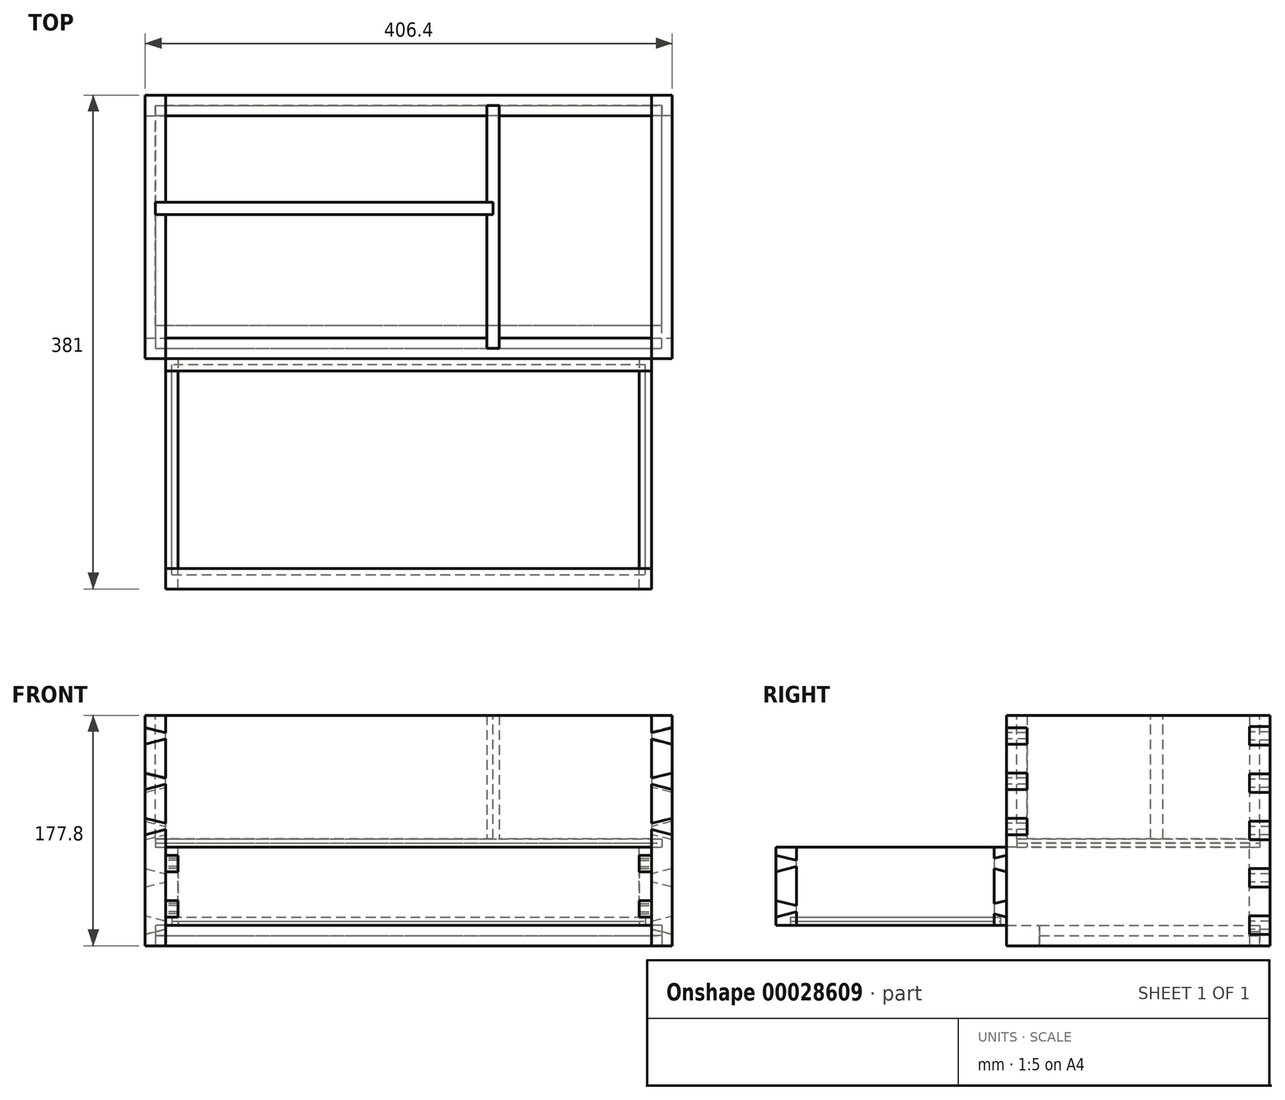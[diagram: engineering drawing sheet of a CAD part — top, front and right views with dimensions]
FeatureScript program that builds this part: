
annotation { "Feature Type Name" : "Feature", "Feature Type Description" : "" }
export const myFeature = defineFeature(function(context is Context, id is Id, definition is map)
    precondition{}
    {
        {
            var Q0;
            Q0=qCreatedBy(makeId("Front.planeOp"),FACE);
            var sketch = newSketch(context, id + "F0", { "sketchPlane" : qUnion([Q0])});
            skLineSegment(sketch, "E0.bottom", {"start": v(0, 0) * mm, "end": v(406.4, 0) * mm});
            skLineSegment(sketch, "E0.top", {"start": v(0, 177.8) * mm, "end": v(406.4, 177.8) * mm});
            skLineSegment(sketch, "E0.left", {"start": v(0, 0) * mm, "end": v(0, 177.8) * mm});
            skLineSegment(sketch, "E0.right", {"start": v(406.4, 0) * mm, "end": v(406.4, 177.8) * mm});
            skSolve(sketch);
        }
        {
            var Q0;
            Q0 = qSketchRegion(id + "F0", true);
            extrude(context, id + "F1", {"entities" : qUnion([Q0]), "depth" : 15.88 * mm});
        }
        {
            var Q0;
            Q0=qCreatedBy(makeId("Front.planeOp"),FACE);
            cPlane(context, id + "F2", {"entities" : qUnion([Q0]), "cplaneType" : CPlaneType.OFFSET, "offset" : 203.2 * mm, "width" : 152.4 * mm, "height" : 152.4 * mm});
        }
        {
            var Q0;
            Q0=qCreatedBy(id+"F2.planeOp",FACE);
            var sketch = newSketch(context, id + "F3", { "sketchPlane" : qUnion([Q0])});
            skLineSegment(sketch, "E1.0", {"start": v(0, 76.2) * mm, "end": v(0, 177.8) * mm});
            skLineSegment(sketch, "E1.1", {"start": v(0, 177.8) * mm, "end": v(406.4, 177.8) * mm});
            skLineSegment(sketch, "E1.2", {"start": v(406.4, 76.2) * mm, "end": v(406.4, 177.8) * mm});
            skLineSegment(sketch, "E2", {"start": v(0, 76.2) * mm, "end": v(406.4, 76.2) * mm});
            skPoint(sketch, "E3.orphan", {"position": v(406.4, 0) * mm});
            skPoint(sketch, "E4.orphan", {"position": v(0, 0) * mm});
            skSolve(sketch);
        }
        {
            var Q0;
            Q0 = qSketchRegion(id + "F3", true);
            extrude(context, id + "F4", {"entities" : qUnion([Q0]), "oppositeDirection" : true, "depth" : 15.88 * mm});
        }
        {
            var Q0;
            Q0=makeQuery(id+"F4.opExtrude","CAP_FACE",FACE,{"disambiguationData":[OSD([sQuery(id+"F3.wireOp",EDGE,"E1.0"),sQuery(id+"F3.wireOp",EDGE,"E1.1"),sQuery(id+"F3.wireOp",EDGE,"E1.2"),sQuery(id+"F3.wireOp",EDGE,"E2")])],"isStart":true});
            var sketch = newSketch(context, id + "F5", { "sketchPlane" : qUnion([Q0])});
            skLineSegment(sketch, "E5", {"start": v(390.53, 177.8) * mm, "end": v(390.53, 164.32) * mm, "construction": true});
            skLineSegment(sketch, "E6", {"start": v(406.4, 168.28) * mm, "end": v(390.52, 164.32) * mm});
            skLineSegment(sketch, "E7", {"start": v(390.52, 159.53) * mm, "end": v(406.4, 155.58) * mm});
            skLineSegment(sketch, "E8.0.1.0", {"start": v(406.4, 133.35) * mm, "end": v(390.53, 129.4) * mm});
            skLineSegment(sketch, "E8.0.1.2", {"start": v(390.53, 124.6) * mm, "end": v(406.4, 120.65) * mm});
            skLineSegment(sketch, "E8.0.1.3", {"start": v(406.4, 120.65) * mm, "end": v(406.4, 133.35) * mm});
            skLineSegment(sketch, "E8.0.2.0", {"start": v(406.4, 98.42) * mm, "end": v(390.53, 94.47) * mm});
            skLineSegment(sketch, "E8.0.2.2", {"start": v(390.53, 89.68) * mm, "end": v(406.4, 85.72) * mm});
            skLineSegment(sketch, "E8.direction2", {"start": v(390.52, 159.53) * mm, "end": v(390.52, 129.4) * mm, "construction": true});
            skLineSegment(sketch, "E9", {"start": v(390.53, 164.32) * mm, "end": v(390.53, 177.8) * mm});
            skLineSegment(sketch, "E10", {"start": v(406.4, 177.8) * mm, "end": v(406.4, 168.28) * mm});
            skLineSegment(sketch, "E11", {"start": v(390.53, 159.53) * mm, "end": v(390.53, 129.4) * mm});
            skLineSegment(sketch, "E12", {"start": v(390.53, 124.6) * mm, "end": v(390.53, 94.47) * mm});
            skLineSegment(sketch, "E13", {"start": v(390.53, 89.68) * mm, "end": v(390.53, 76.2) * mm});
            skLineSegment(sketch, "E14", {"start": v(406.4, 76.2) * mm, "end": v(406.4, 85.72) * mm});
            skLineSegment(sketch, "E15", {"start": v(406.4, 98.42) * mm, "end": v(406.4, 120.65) * mm});
            skLineSegment(sketch, "E16", {"start": v(406.4, 133.35) * mm, "end": v(406.4, 155.58) * mm});
            skLineSegment(sketch, "E17.trimOffspring", {"start": v(390.53, 159.53) * mm, "end": v(390.53, 76.2) * mm, "construction": true});
            skLineSegment(sketch, "E18", {"start": v(203.2, 177.8) * mm, "end": v(203.2, 76.2) * mm, "construction": true});
            skLineSegment(sketch, "E19.MirrorCS", {"start": v(15.88, 159.53) * mm, "end": v(15.88, 129.4) * mm});
            skLineSegment(sketch, "E20.MirrorCS", {"start": v(15.88, 89.68) * mm, "end": v(15.88, 76.2) * mm});
            skLineSegment(sketch, "E21.MirrorCS", {"start": v(15.88, 89.68) * mm, "end": v(0, 85.73) * mm});
            skLineSegment(sketch, "E22.MirrorCS", {"start": v(15.88, 177.8) * mm, "end": v(15.88, 164.32) * mm});
            skLineSegment(sketch, "E23.MirrorCS", {"start": v(15.88, 124.6) * mm, "end": v(0, 120.65) * mm});
            skLineSegment(sketch, "E24.MirrorCS", {"start": v(0, 76.2) * mm, "end": v(0, 85.73) * mm});
            skLineSegment(sketch, "E25.MirrorCS", {"start": v(15.88, 124.6) * mm, "end": v(15.88, 94.47) * mm});
            skLineSegment(sketch, "E26.MirrorCS", {"start": v(0, 133.35) * mm, "end": v(0, 155.58) * mm});
            skLineSegment(sketch, "E27.MirrorCS", {"start": v(0, 177.8) * mm, "end": v(0, 168.28) * mm});
            skLineSegment(sketch, "E28.MirrorCS", {"start": v(15.88, 164.32) * mm, "end": v(15.88, 177.8) * mm});
            skLineSegment(sketch, "E29.MirrorCS", {"start": v(0, 98.43) * mm, "end": v(15.88, 94.47) * mm});
            skLineSegment(sketch, "E30.MirrorCS", {"start": v(0, 98.43) * mm, "end": v(0, 120.65) * mm});
            skLineSegment(sketch, "E31.MirrorCS", {"start": v(0, 168.28) * mm, "end": v(15.88, 164.32) * mm});
            skLineSegment(sketch, "E32.MirrorCS", {"start": v(0, 120.65) * mm, "end": v(0, 133.35) * mm});
            skLineSegment(sketch, "E33.MirrorCS", {"start": v(0, 133.35) * mm, "end": v(15.88, 129.4) * mm});
            skLineSegment(sketch, "E34.MirrorCS", {"start": v(15.88, 159.53) * mm, "end": v(0, 155.58) * mm});
            skSolve(sketch);
        }
        {
            var Q0;
            Q0 = qSketchRegion(id + "F5", true);
            var Q1;
            Q1=makeQuery(id+"F5.imprint","IMPRINT",FACE,{"disambiguationData":[TD([[makeQuery(id+"F5.imprint","IMPRINT",EDGE,{"derivedFrom":sQuery(id+"F5.wireOp",EDGE,"E6")}),-1.0]])]});
            var Q2;
            Q2=makeQuery(id+"F5.imprint","IMPRINT",FACE,{"disambiguationData":[TD([[makeQuery(id+"F5.imprint","IMPRINT",EDGE,{"derivedFrom":sQuery(id+"F5.wireOp",EDGE,"E8.0.2.2")}),-1.0]])]});
            var Q3;
            {var subQ2=sQuery(id+"F5.wireOp",EDGE,"E27.MirrorCS");Q3=makeQuery(id+"F5.imprint","IMPRINT",FACE,{"disambiguationData":[TD([[makeQuery(id+"F5.imprint","IMPRINT",EDGE,{"derivedFrom":subQ2}),-1.0]])]});}
            var Q4;
            Q4=makeQuery(id+"F5.imprint","IMPRINT",FACE,{"disambiguationData":[TD([[makeQuery(id+"F5.imprint","IMPRINT",EDGE,{"derivedFrom":sQuery(id+"F5.wireOp",EDGE,"E21.MirrorCS")}),1.0]])]});
            extrude(context, id + "F6", {"entities" : qUnion([Q0, Q1, Q2, Q3, Q4]), "operationType" : NewBodyOperationType.REMOVE, "endBound" : BoundingType.UP_TO_NEXT, "oppositeDirection" : true, "depth" : 25.4 * mm});
        }
        {
            var Q0;
            Q0=qCreatedBy(makeId("Right.planeOp"),FACE);
            cPlane(context, id + "F7", {"entities" : qUnion([Q0]), "cplaneType" : CPlaneType.OFFSET, "offset" : 406.4 * mm, "width" : 152.4 * mm, "height" : 152.4 * mm});
        }
        {
            var Q0;
            Q0=makeQuery(id+"F1.opExtrude","CAP_FACE",FACE,{"disambiguationData":[OSD([sQuery(id+"F0.wireOp",EDGE,"E0.bottom"),sQuery(id+"F0.wireOp",EDGE,"E0.top"),sQuery(id+"F0.wireOp",EDGE,"E0.left"),sQuery(id+"F0.wireOp",EDGE,"E0.right")])],"isStart":false});
            var sketch = newSketch(context, id + "F8", { "sketchPlane" : qUnion([Q0])});
            skLineSegment(sketch, "E35", {"start": v(203.2, 177.8) * mm, "end": v(203.2, 0) * mm, "construction": true});
            skLineSegment(sketch, "E36", {"start": v(390.53, 177.8) * mm, "end": v(390.53, 165.11) * mm});
            skLineSegment(sketch, "E37", {"start": v(406.4, 88.9) * mm, "end": v(203.2, 88.9) * mm, "construction": true});
            skLineSegment(sketch, "E38", {"start": v(390.53, 177.8) * mm, "end": v(406.4, 177.8) * mm});
            skLineSegment(sketch, "E39", {"start": v(406.4, 177.8) * mm, "end": v(406.4, 169.07) * mm});
            skLineSegment(sketch, "E40", {"start": v(406.4, 169.07) * mm, "end": v(390.53, 165.11) * mm});
            skLineSegment(sketch, "E41", {"start": v(390.53, 158.74) * mm, "end": v(406.4, 154.78) * mm});
            skLineSegment(sketch, "E42", {"start": v(406.4, 154.78) * mm, "end": v(406.4, 132.56) * mm});
            skLineSegment(sketch, "E43", {"start": v(406.4, 132.56) * mm, "end": v(390.53, 128.6) * mm});
            skLineSegment(sketch, "E44.trimOffspring", {"start": v(390.53, 158.74) * mm, "end": v(390.53, 128.6) * mm});
            skLineSegment(sketch, "E45", {"start": v(406.4, 118.27) * mm, "end": v(390.53, 122.23) * mm});
            skLineSegment(sketch, "E46", {"start": v(406.4, 96.04) * mm, "end": v(390.53, 92.09) * mm});
            skLineSegment(sketch, "E47", {"start": v(406.4, 118.27) * mm, "end": v(406.4, 96.04) * mm});
            skPoint(sketch, "E48.orphan", {"position": v(390.53, 0) * mm});
            skLineSegment(sketch, "E49.trimOffspring", {"start": v(390.53, 122.23) * mm, "end": v(390.53, 92.09) * mm});
            skLineSegment(sketch, "E50.MirrorCS", {"start": v(390.53, 0) * mm, "end": v(406.4, 0) * mm});
            skLineSegment(sketch, "E51.MirrorCS", {"start": v(406.4, 8.73) * mm, "end": v(390.53, 12.69) * mm});
            skLineSegment(sketch, "E52.MirrorCS", {"start": v(406.4, 0) * mm, "end": v(406.4, 8.73) * mm});
            skLineSegment(sketch, "E53.MirrorCS", {"start": v(406.4, 59.53) * mm, "end": v(406.4, 81.76) * mm});
            skLineSegment(sketch, "E54.MirrorCS", {"start": v(406.4, 23.02) * mm, "end": v(406.4, 45.24) * mm});
            skLineSegment(sketch, "E55.MirrorCS", {"start": v(390.53, 19.06) * mm, "end": v(406.4, 23.02) * mm});
            skLineSegment(sketch, "E56.MirrorCS", {"start": v(390.53, 19.06) * mm, "end": v(390.53, 49.2) * mm});
            skLineSegment(sketch, "E57.MirrorCS", {"start": v(390.53, 0) * mm, "end": v(390.53, 12.69) * mm});
            skLineSegment(sketch, "E58.MirrorCS", {"start": v(406.4, 59.53) * mm, "end": v(390.53, 55.57) * mm});
            skLineSegment(sketch, "E59.MirrorCS", {"start": v(390.53, 55.57) * mm, "end": v(390.53, 85.71) * mm});
            skLineSegment(sketch, "E60.MirrorCS", {"start": v(406.4, 45.24) * mm, "end": v(390.53, 49.2) * mm});
            skLineSegment(sketch, "E61.MirrorCS", {"start": v(406.4, 81.76) * mm, "end": v(390.53, 85.71) * mm});
            skLineSegment(sketch, "E62.MirrorCS", {"start": v(15.88, 177.8) * mm, "end": v(15.88, 165.11) * mm});
            skPoint(sketch, "E63.MirrorP", {"position": v(15.88, 0) * mm});
            skLineSegment(sketch, "E64.MirrorCS", {"start": v(15.87, 19.06) * mm, "end": v(0, 23.02) * mm});
            skLineSegment(sketch, "E65.MirrorCS", {"start": v(15.88, 0) * mm, "end": v(15.88, 12.69) * mm});
            skLineSegment(sketch, "E66.MirrorCS", {"start": v(0, 59.53) * mm, "end": v(0, 81.76) * mm});
            skLineSegment(sketch, "E67.MirrorCS", {"start": v(0, 177.8) * mm, "end": v(0, 169.07) * mm});
            skLineSegment(sketch, "E68.MirrorCS", {"start": v(0, 169.07) * mm, "end": v(15.88, 165.11) * mm});
            skLineSegment(sketch, "E69.MirrorCS", {"start": v(0, 96.04) * mm, "end": v(15.88, 92.09) * mm});
            skLineSegment(sketch, "E70.MirrorCS", {"start": v(0, 118.27) * mm, "end": v(0, 96.04) * mm});
            skLineSegment(sketch, "E71.MirrorCS", {"start": v(15.88, 158.74) * mm, "end": v(15.88, 128.6) * mm});
            skLineSegment(sketch, "E72.MirrorCS", {"start": v(0, 118.27) * mm, "end": v(15.88, 122.23) * mm});
            skLineSegment(sketch, "E73.MirrorCS", {"start": v(15.87, 55.57) * mm, "end": v(15.87, 85.71) * mm});
            skLineSegment(sketch, "E74.MirrorCS", {"start": v(0, 132.56) * mm, "end": v(15.88, 128.6) * mm});
            skLineSegment(sketch, "E75.MirrorCS", {"start": v(15.88, 158.74) * mm, "end": v(0, 154.78) * mm});
            skLineSegment(sketch, "E76.MirrorCS", {"start": v(0, 154.78) * mm, "end": v(0, 132.56) * mm});
            skLineSegment(sketch, "E77.MirrorCS", {"start": v(15.88, 177.8) * mm, "end": v(0, 177.8) * mm});
            skLineSegment(sketch, "E78.MirrorCS", {"start": v(0, 59.53) * mm, "end": v(15.87, 55.57) * mm});
            skLineSegment(sketch, "E79.MirrorCS", {"start": v(15.87, 0) * mm, "end": v(0, 0) * mm});
            skLineSegment(sketch, "E80.MirrorCS", {"start": v(0, 8.73) * mm, "end": v(15.87, 12.69) * mm});
            skLineSegment(sketch, "E81.MirrorCS", {"start": v(15.88, 19.06) * mm, "end": v(15.88, 49.2) * mm});
            skLineSegment(sketch, "E82.MirrorCS", {"start": v(0, 23.02) * mm, "end": v(0, 45.24) * mm});
            skLineSegment(sketch, "E83.MirrorCS", {"start": v(0, 0) * mm, "end": v(0, 8.73) * mm});
            skLineSegment(sketch, "E84.MirrorCS", {"start": v(0, 45.24) * mm, "end": v(15.87, 49.2) * mm});
            skLineSegment(sketch, "E85.MirrorCS", {"start": v(15.88, 122.23) * mm, "end": v(15.88, 92.09) * mm});
            skLineSegment(sketch, "E86.MirrorCS", {"start": v(0, 81.76) * mm, "end": v(15.88, 85.71) * mm});
            skSolve(sketch);
        }
        {
            var Q0;
            Q0 = qSketchRegion(id + "F8", true);
            extrude(context, id + "F9", {"entities" : qUnion([Q0]), "operationType" : NewBodyOperationType.REMOVE, "endBound" : BoundingType.UP_TO_NEXT, "oppositeDirection" : true, "depth" : 25.4 * mm});
        }
        {
            var Q0;
            Q0=qCreatedBy(makeId("Right.planeOp"),FACE);
            cPlane(context, id + "F10", {"entities" : qUnion([Q0]), "cplaneType" : CPlaneType.OFFSET, "offset" : 203.2 * mm, "width" : 152.4 * mm, "height" : 152.4 * mm});
        }
        {
            var Q0;
            Q0=qCreatedBy(id+"F7.planeOp",FACE);
            var sketch = newSketch(context, id + "F11", { "sketchPlane" : qUnion([Q0])});
            skLineSegment(sketch, "E87.0", {"start": v(0, 0) * mm, "end": v(0, 177.8) * mm});
            skLineSegment(sketch, "E88.0", {"start": v(-203.2, 159.53) * mm, "end": v(-203.2, 129.4) * mm});
            skLineSegment(sketch, "E89", {"start": v(-203.2, 159.53) * mm, "end": v(-203.2, 177.8) * mm});
            skLineSegment(sketch, "E90", {"start": v(-203.2, 177.8) * mm, "end": v(0, 177.8) * mm});
            skLineSegment(sketch, "E91", {"start": v(-203.2, 129.4) * mm, "end": v(-203.2, 0) * mm});
            skLineSegment(sketch, "E92", {"start": v(-203.2, 0) * mm, "end": v(0, 0) * mm});
            skSolve(sketch);
        }
        {
            var Q0;
            Q0 = qSketchRegion(id + "F11", true);
            extrude(context, id + "F12", {"entities" : qUnion([Q0]), "oppositeDirection" : true, "depth" : 15.88 * mm});
        }
        {
            var Q0;
            Q0=makeQuery(id+"F12.opExtrude","SWEPT_BODY",BODY,{"disambiguationData":[OSD([sQuery(id+"F11.wireOp",EDGE,"E87.0"),sQuery(id+"F11.wireOp",EDGE,"E88.0"),sQuery(id+"F11.wireOp",EDGE,"E89"),sQuery(id+"F11.wireOp",EDGE,"E90"),sQuery(id+"F11.wireOp",EDGE,"E91"),sQuery(id+"F11.wireOp",EDGE,"E92")])]});
            var Q1;
            Q1=qCreatedBy(id+"F10.planeOp",FACE);
            mirror(context, id + "F13", {"entities" : qUnion([Q0]), "mirrorPlane" : qUnion([Q1])});
        }
        {
            var Q0;
            Q0=makeQuery(id+"F1.opExtrude","SWEPT_BODY",BODY,{"disambiguationData":[OSD([sQuery(id+"F0.wireOp",EDGE,"E0.bottom"),sQuery(id+"F0.wireOp",EDGE,"E0.top"),sQuery(id+"F0.wireOp",EDGE,"E0.left"),sQuery(id+"F0.wireOp",EDGE,"E0.right")])]});
            var Q1;
            Q1=makeQuery(id+"F12.opExtrude","SWEPT_BODY",BODY,{"disambiguationData":[OSD([sQuery(id+"F11.wireOp",EDGE,"E87.0"),sQuery(id+"F11.wireOp",EDGE,"E88.0"),sQuery(id+"F11.wireOp",EDGE,"E89"),sQuery(id+"F11.wireOp",EDGE,"E90"),sQuery(id+"F11.wireOp",EDGE,"E91"),sQuery(id+"F11.wireOp",EDGE,"E92")])]});
            var Q2;
            Q2=makeQuery(id+"F13.opPattern","COPY",BODY,{"derivedFrom":makeQuery(id+"F12.opExtrude","SWEPT_BODY",BODY,{"disambiguationData":[OSD([sQuery(id+"F11.wireOp",EDGE,"E87.0"),sQuery(id+"F11.wireOp",EDGE,"E88.0"),sQuery(id+"F11.wireOp",EDGE,"E89"),sQuery(id+"F11.wireOp",EDGE,"E90"),sQuery(id+"F11.wireOp",EDGE,"E91"),sQuery(id+"F11.wireOp",EDGE,"E92")])]}),"instanceName":"1"});
            booleanBodies(context, id + "F14", {"operationType" : BooleanOperationType.SUBTRACTION, "tools" : qUnion([Q0]), "targets" : qUnion([Q1, Q2]), "keepTools" : true});
        }
        {
            var Q0;
            Q0=makeQuery(id+"F4.opExtrude","SWEPT_BODY",BODY,{"disambiguationData":[OSD([sQuery(id+"F3.wireOp",EDGE,"E1.0"),sQuery(id+"F3.wireOp",EDGE,"E1.1"),sQuery(id+"F3.wireOp",EDGE,"E1.2"),sQuery(id+"F3.wireOp",EDGE,"E2")])]});
            var Q1;
            Q1=makeQuery(id+"F12.opExtrude","SWEPT_BODY",BODY,{"disambiguationData":[OSD([sQuery(id+"F11.wireOp",EDGE,"E87.0"),sQuery(id+"F11.wireOp",EDGE,"E88.0"),sQuery(id+"F11.wireOp",EDGE,"E89"),sQuery(id+"F11.wireOp",EDGE,"E90"),sQuery(id+"F11.wireOp",EDGE,"E91"),sQuery(id+"F11.wireOp",EDGE,"E92")])]});
            var Q2;
            Q2=makeQuery(id+"F13.opPattern","COPY",BODY,{"derivedFrom":makeQuery(id+"F12.opExtrude","SWEPT_BODY",BODY,{"disambiguationData":[OSD([sQuery(id+"F11.wireOp",EDGE,"E87.0"),sQuery(id+"F11.wireOp",EDGE,"E88.0"),sQuery(id+"F11.wireOp",EDGE,"E89"),sQuery(id+"F11.wireOp",EDGE,"E90"),sQuery(id+"F11.wireOp",EDGE,"E91"),sQuery(id+"F11.wireOp",EDGE,"E92")])]}),"instanceName":"1"});
            booleanBodies(context, id + "F15", {"operationType" : BooleanOperationType.SUBTRACTION, "tools" : qUnion([Q0]), "targets" : qUnion([Q1, Q2]), "keepTools" : true});
        }
        {
            var Q0;
            Q0=qCreatedBy(makeId("Top.planeOp"),FACE);
            var sketch = newSketch(context, id + "F16", { "sketchPlane" : qUnion([Q0])});
            skPoint(sketch, "E93.orphan", {"position": v(15.88, 0) * mm});
            skPoint(sketch, "E94.orphan", {"position": v(390.53, 0) * mm});
            skPoint(sketch, "E95.orphan", {"position": v(15.88, -203.2) * mm});
            skPoint(sketch, "E96.orphan", {"position": v(390.53, -203.2) * mm});
            skLineSegment(sketch, "E97.0", {"start": v(7.94, -177.8) * mm, "end": v(7.94, -7.94) * mm});
            skLineSegment(sketch, "E97.1", {"start": v(7.94, -7.94) * mm, "end": v(398.46, -7.94) * mm});
            skLineSegment(sketch, "E97.2", {"start": v(398.46, -177.8) * mm, "end": v(398.46, -7.94) * mm});
            skPoint(sketch, "E98.1.end.orphan", {"position": v(390.53, -15.88) * mm});
            skPoint(sketch, "E98.0.end.orphan", {"position": v(15.87, -15.88) * mm});
            skLineSegment(sketch, "E99", {"start": v(398.46, -177.8) * mm, "end": v(7.94, -177.8) * mm});
            skSolve(sketch);
        }
        {
            var Q0;
            Q0 = qSketchRegion(id + "F16", true);
            extrude(context, id + "F17", {"entities" : qUnion([Q0]), "depth" : 15.88 * mm});
        }
        {
            var Q0;
            Q0=makeQuery(id+"F17.opExtrude","CAP_FACE",FACE,{"disambiguationData":[OSD([sQuery(id+"F16.wireOp",EDGE,"E97.0"),sQuery(id+"F16.wireOp",EDGE,"E97.1"),sQuery(id+"F16.wireOp",EDGE,"E97.2"),sQuery(id+"F16.wireOp",EDGE,"E99")])],"isStart":true});
            var sketch = newSketch(context, id + "F18", { "sketchPlane" : qUnion([Q0])});
            skLineSegment(sketch, "E100", {"start": v(15.88, 177.8) * mm, "end": v(15.88, 15.88) * mm});
            skLineSegment(sketch, "E101", {"start": v(15.88, 15.88) * mm, "end": v(390.53, 15.88) * mm});
            skLineSegment(sketch, "E102", {"start": v(390.53, 177.8) * mm, "end": v(390.53, 15.88) * mm});
            skLineSegment(sketch, "E103", {"start": v(15.88, 177.8) * mm, "end": v(7.94, 177.8) * mm});
            skLineSegment(sketch, "E104", {"start": v(7.94, 177.8) * mm, "end": v(7.94, 7.94) * mm});
            skLineSegment(sketch, "E105", {"start": v(7.94, 7.94) * mm, "end": v(398.46, 7.94) * mm});
            skLineSegment(sketch, "E106", {"start": v(398.46, 7.94) * mm, "end": v(398.46, 177.8) * mm});
            skLineSegment(sketch, "E107", {"start": v(398.46, 177.8) * mm, "end": v(390.53, 177.8) * mm});
            skSolve(sketch);
        }
        {
            var Q0;
            Q0 = qSketchRegion(id + "F18", true);
            extrude(context, id + "F19", {"entities" : qUnion([Q0]), "operationType" : NewBodyOperationType.REMOVE, "oppositeDirection" : true, "depth" : 7.94 * mm});
        }
        {
            var Q0;
            Q0=makeQuery(id+"F17.opExtrude","SWEPT_BODY",BODY,{"disambiguationData":[OSD([sQuery(id+"F16.wireOp",EDGE,"E97.0"),sQuery(id+"F16.wireOp",EDGE,"E97.1"),sQuery(id+"F16.wireOp",EDGE,"E97.2"),sQuery(id+"F16.wireOp",EDGE,"E99")])]});
            var Q1;
            Q1=makeQuery(id+"F13.opPattern","COPY",BODY,{"derivedFrom":makeQuery(id+"F12.opExtrude","SWEPT_BODY",BODY,{"disambiguationData":[OSD([sQuery(id+"F11.wireOp",EDGE,"E87.0"),sQuery(id+"F11.wireOp",EDGE,"E88.0"),sQuery(id+"F11.wireOp",EDGE,"E89"),sQuery(id+"F11.wireOp",EDGE,"E90"),sQuery(id+"F11.wireOp",EDGE,"E91"),sQuery(id+"F11.wireOp",EDGE,"E92")])]}),"instanceName":"1"});
            var Q2;
            Q2=makeQuery(id+"F1.opExtrude","SWEPT_BODY",BODY,{"disambiguationData":[OSD([sQuery(id+"F0.wireOp",EDGE,"E0.bottom"),sQuery(id+"F0.wireOp",EDGE,"E0.top"),sQuery(id+"F0.wireOp",EDGE,"E0.left"),sQuery(id+"F0.wireOp",EDGE,"E0.right")])]});
            booleanBodies(context, id + "F20", {"operationType" : BooleanOperationType.SUBTRACTION, "tools" : qUnion([Q0]), "targets" : qUnion([Q1, Q2]), "keepTools" : true});
        }
        {
            var Q0;
            Q0=makeQuery(id+"F17.opExtrude","SWEPT_FACE",FACE,{"disambiguationData":[OSD([sQuery(id+"F16.wireOp",EDGE,"E99")])]});
            var sketch = newSketch(context, id + "F21", { "sketchPlane" : qUnion([Q0])});
            skLineSegment(sketch, "E108.0", {"start": v(15.88, 0) * mm, "end": v(390.53, 0) * mm});
            skLineSegment(sketch, "E108.1", {"start": v(390.53, 15.88) * mm, "end": v(15.88, 15.88) * mm});
            skLineSegment(sketch, "E108.2", {"start": v(15.88, 0) * mm, "end": v(15.88, 15.88) * mm});
            skLineSegment(sketch, "E108.3", {"start": v(390.53, 0) * mm, "end": v(390.53, 15.88) * mm});
            skPoint(sketch, "E109.orphan", {"position": v(0, 0) * mm});
            skPoint(sketch, "E110.orphan", {"position": v(7.94, 15.88) * mm});
            skPoint(sketch, "E111.orphan", {"position": v(398.46, 15.88) * mm});
            skPoint(sketch, "E112.orphan", {"position": v(406.4, 0) * mm});
            skPoint(sketch, "E113.orphan", {"position": v(390.53, 89.68) * mm});
            skPoint(sketch, "E114.orphan", {"position": v(15.88, 89.68) * mm});
            skSolve(sketch);
        }
        {
            var Q0;
            Q0 = qSketchRegion(id + "F21", true);
            extrude(context, id + "F22", {"entities" : qUnion([Q0]), "depth" : 25.4 * mm});
        }
        {
            var Q0;
            Q0=qCreatedBy(makeId("Top.planeOp"),FACE);
            cPlane(context, id + "F23", {"entities" : qUnion([Q0]), "cplaneType" : CPlaneType.OFFSET, "offset" : 76.2 * mm, "width" : 152.4 * mm, "height" : 152.4 * mm});
        }
        {
            var Q0;
            Q0=qCreatedBy(id+"F23.planeOp",FACE);
            var sketch = newSketch(context, id + "F24", { "sketchPlane" : qUnion([Q0])});
            skPoint(sketch, "E115.orphan", {"position": v(15.88, -203.2) * mm});
            skPoint(sketch, "E116.orphan", {"position": v(390.53, -203.2) * mm});
            skPoint(sketch, "E117.orphan", {"position": v(390.53, 0) * mm});
            skPoint(sketch, "E118.orphan", {"position": v(15.88, 0) * mm});
            skLineSegment(sketch, "E119.0", {"start": v(15.88, -195.26) * mm, "end": v(390.53, -195.26) * mm});
            skLineSegment(sketch, "E120.0", {"start": v(384.18, -193.67) * mm, "end": v(384.18, -196.85) * mm});
            skLineSegment(sketch, "E121.0", {"start": v(7.94, -187.33) * mm, "end": v(7.94, -15.88) * mm});
            skLineSegment(sketch, "E122.0", {"start": v(15.87, -7.94) * mm, "end": v(390.53, -7.94) * mm});
            skLineSegment(sketch, "E123.0", {"start": v(398.46, -187.33) * mm, "end": v(398.46, -15.88) * mm});
            skLineSegment(sketch, "E124", {"start": v(390.53, -195.26) * mm, "end": v(398.46, -195.26) * mm});
            skLineSegment(sketch, "E125", {"start": v(398.46, -195.26) * mm, "end": v(398.46, -187.33) * mm});
            skLineSegment(sketch, "E126", {"start": v(398.46, -15.88) * mm, "end": v(398.46, -7.94) * mm});
            skLineSegment(sketch, "E127", {"start": v(398.46, -7.94) * mm, "end": v(390.53, -7.94) * mm});
            skLineSegment(sketch, "E128", {"start": v(15.87, -7.94) * mm, "end": v(7.94, -7.94) * mm});
            skLineSegment(sketch, "E129", {"start": v(7.94, -7.94) * mm, "end": v(7.94, -15.88) * mm});
            skLineSegment(sketch, "E130", {"start": v(7.94, -187.33) * mm, "end": v(7.94, -195.26) * mm});
            skLineSegment(sketch, "E131", {"start": v(7.94, -195.26) * mm, "end": v(15.88, -195.26) * mm});
            skPoint(sketch, "E132.1.start.orphan", {"position": v(15.88, -187.33) * mm});
            skPoint(sketch, "E132.2.start.orphan", {"position": v(15.87, -15.88) * mm});
            skPoint(sketch, "E132.3.end.orphan", {"position": v(390.53, -15.88) * mm});
            skPoint(sketch, "E132.3.start.orphan", {"position": v(390.53, -187.33) * mm});
            skSolve(sketch);
        }
        {
            var Q0;
            Q0 = qSketchRegion(id + "F24", true);
            extrude(context, id + "F25", {"entities" : qUnion([Q0]), "depth" : 6.35 * mm});
        }
        {
            var Q0;
            Q0=makeQuery(id+"F25.opExtrude","CAP_FACE",FACE,{"disambiguationData":[OSD([sQuery(id+"F24.wireOp",EDGE,"E119.0"),sQuery(id+"F24.wireOp",EDGE,"E121.0"),sQuery(id+"F24.wireOp",EDGE,"E122.0"),sQuery(id+"F24.wireOp",EDGE,"E123.0"),sQuery(id+"F24.wireOp",EDGE,"E124"),sQuery(id+"F24.wireOp",EDGE,"E125"),sQuery(id+"F24.wireOp",EDGE,"E126"),sQuery(id+"F24.wireOp",EDGE,"E127"),sQuery(id+"F24.wireOp",EDGE,"E128"),sQuery(id+"F24.wireOp",EDGE,"E129"),sQuery(id+"F24.wireOp",EDGE,"E130"),sQuery(id+"F24.wireOp",EDGE,"E131")])],"isStart":true});
            var sketch = newSketch(context, id + "F26", { "sketchPlane" : qUnion([Q0])});
            skLineSegment(sketch, "E133.0", {"start": v(15.88, 187.33) * mm, "end": v(390.53, 187.33) * mm});
            skLineSegment(sketch, "E133.1", {"start": v(15.88, 15.87) * mm, "end": v(15.88, 187.33) * mm});
            skLineSegment(sketch, "E133.2", {"start": v(390.53, 15.87) * mm, "end": v(15.88, 15.87) * mm});
            skLineSegment(sketch, "E133.3", {"start": v(390.53, 187.33) * mm, "end": v(390.53, 15.88) * mm});
            skLineSegment(sketch, "E134.0", {"start": v(7.94, 195.26) * mm, "end": v(398.46, 195.26) * mm});
            skLineSegment(sketch, "E134.1", {"start": v(7.94, 7.94) * mm, "end": v(7.94, 195.26) * mm});
            skLineSegment(sketch, "E134.2", {"start": v(398.46, 7.94) * mm, "end": v(7.94, 7.94) * mm});
            skLineSegment(sketch, "E134.3", {"start": v(398.46, 195.26) * mm, "end": v(398.46, 7.94) * mm});
            skSolve(sketch);
        }
        {
            var Q0;
            Q0 = qSketchRegion(id + "F26", true);
            extrude(context, id + "F27", {"entities" : qUnion([Q0]), "operationType" : NewBodyOperationType.REMOVE, "oppositeDirection" : true, "depth" : 3.17 * mm});
        }
        {
            var Q0;
            Q0=makeQuery(id+"F25.opExtrude","SWEPT_BODY",BODY,{"disambiguationData":[OSD([sQuery(id+"F24.wireOp",EDGE,"E119.0"),sQuery(id+"F24.wireOp",EDGE,"E121.0"),sQuery(id+"F24.wireOp",EDGE,"E122.0"),sQuery(id+"F24.wireOp",EDGE,"E123.0"),sQuery(id+"F24.wireOp",EDGE,"E124"),sQuery(id+"F24.wireOp",EDGE,"E125"),sQuery(id+"F24.wireOp",EDGE,"E126"),sQuery(id+"F24.wireOp",EDGE,"E127"),sQuery(id+"F24.wireOp",EDGE,"E128"),sQuery(id+"F24.wireOp",EDGE,"E129"),sQuery(id+"F24.wireOp",EDGE,"E130"),sQuery(id+"F24.wireOp",EDGE,"E131")])]});
            var Q1;
            Q1=makeQuery(id+"F13.opPattern","COPY",BODY,{"derivedFrom":makeQuery(id+"F12.opExtrude","SWEPT_BODY",BODY,{"disambiguationData":[OSD([sQuery(id+"F11.wireOp",EDGE,"E87.0"),sQuery(id+"F11.wireOp",EDGE,"E88.0"),sQuery(id+"F11.wireOp",EDGE,"E89"),sQuery(id+"F11.wireOp",EDGE,"E90"),sQuery(id+"F11.wireOp",EDGE,"E91"),sQuery(id+"F11.wireOp",EDGE,"E92")])]}),"instanceName":"1"});
            var Q2;
            Q2=makeQuery(id+"F1.opExtrude","SWEPT_BODY",BODY,{"disambiguationData":[OSD([sQuery(id+"F0.wireOp",EDGE,"E0.bottom"),sQuery(id+"F0.wireOp",EDGE,"E0.top"),sQuery(id+"F0.wireOp",EDGE,"E0.left"),sQuery(id+"F0.wireOp",EDGE,"E0.right")])]});
            var Q3;
            Q3=makeQuery(id+"F12.opExtrude","SWEPT_BODY",BODY,{"disambiguationData":[OSD([sQuery(id+"F11.wireOp",EDGE,"E87.0"),sQuery(id+"F11.wireOp",EDGE,"E88.0"),sQuery(id+"F11.wireOp",EDGE,"E89"),sQuery(id+"F11.wireOp",EDGE,"E90"),sQuery(id+"F11.wireOp",EDGE,"E91"),sQuery(id+"F11.wireOp",EDGE,"E92")])]});
            var Q4;
            Q4=makeQuery(id+"F4.opExtrude","SWEPT_BODY",BODY,{"disambiguationData":[OSD([sQuery(id+"F3.wireOp",EDGE,"E1.0"),sQuery(id+"F3.wireOp",EDGE,"E1.1"),sQuery(id+"F3.wireOp",EDGE,"E1.2"),sQuery(id+"F3.wireOp",EDGE,"E2")])]});
            booleanBodies(context, id + "F28", {"operationType" : BooleanOperationType.SUBTRACTION, "tools" : qUnion([Q0]), "targets" : qUnion([Q1, Q2, Q3, Q4]), "keepTools" : true});
        }
        {
            var Q0;
            Q0=makeQuery(id+"F4.opExtrude","SWEPT_FACE",FACE,{"disambiguationData":[OSD([sQuery(id+"F3.wireOp",EDGE,"E1.1")])]});
            var sketch = newSketch(context, id + "F29", { "sketchPlane" : qUnion([Q0])});
            skLineSegment(sketch, "E135.bottom", {"start": v(273.05, -7.94) * mm, "end": v(263.53, -7.94) * mm});
            skLineSegment(sketch, "E135.top", {"start": v(273.05, -195.26) * mm, "end": v(263.53, -195.26) * mm});
            skLineSegment(sketch, "E135.left", {"start": v(273.05, -7.94) * mm, "end": v(273.05, -195.26) * mm});
            skLineSegment(sketch, "E135.right", {"start": v(263.53, -7.94) * mm, "end": v(263.53, -195.26) * mm});
            skSolve(sketch);
        }
        {
            var Q0;
            Q0 = qSketchRegion(id + "F29", true);
            extrude(context, id + "F30", {"entities" : qUnion([Q0]), "endBound" : BoundingType.UP_TO_NEXT, "oppositeDirection" : true, "depth" : 25.4 * mm});
        }
        {
            var Q0;
            Q0=makeQuery(id+"F30.opExtrude","SWEPT_BODY",BODY,{"disambiguationData":[OSD([sQuery(id+"F29.wireOp",EDGE,"E135.bottom"),sQuery(id+"F29.wireOp",EDGE,"E135.top"),sQuery(id+"F29.wireOp",EDGE,"E135.left"),sQuery(id+"F29.wireOp",EDGE,"E135.right")])]});
            var Q1;
            Q1=makeQuery(id+"F1.opExtrude","SWEPT_BODY",BODY,{"disambiguationData":[OSD([sQuery(id+"F0.wireOp",EDGE,"E0.bottom"),sQuery(id+"F0.wireOp",EDGE,"E0.top"),sQuery(id+"F0.wireOp",EDGE,"E0.left"),sQuery(id+"F0.wireOp",EDGE,"E0.right")])]});
            var Q2;
            Q2=makeQuery(id+"F4.opExtrude","SWEPT_BODY",BODY,{"disambiguationData":[OSD([sQuery(id+"F3.wireOp",EDGE,"E1.0"),sQuery(id+"F3.wireOp",EDGE,"E1.1"),sQuery(id+"F3.wireOp",EDGE,"E1.2"),sQuery(id+"F3.wireOp",EDGE,"E2")])]});
            booleanBodies(context, id + "F31", {"operationType" : BooleanOperationType.SUBTRACTION, "tools" : qUnion([Q0]), "targets" : qUnion([Q1, Q2]), "keepTools" : true});
        }
        {
            var Q0;
            Q0=makeQuery(id+"F4.opExtrude","SWEPT_FACE",FACE,{"disambiguationData":[OSD([sQuery(id+"F3.wireOp",EDGE,"E1.1")])]});
            var sketch = newSketch(context, id + "F32", { "sketchPlane" : qUnion([Q0])});
            skLineSegment(sketch, "E136.bottom", {"start": v(7.94, -82.55) * mm, "end": v(268.29, -82.55) * mm});
            skLineSegment(sketch, "E136.top", {"start": v(7.94, -92.07) * mm, "end": v(268.29, -92.07) * mm});
            skLineSegment(sketch, "E136.left", {"start": v(7.94, -82.55) * mm, "end": v(7.94, -92.07) * mm});
            skLineSegment(sketch, "E136.right", {"start": v(268.29, -82.55) * mm, "end": v(268.29, -92.07) * mm});
            skSolve(sketch);
        }
        {
            var Q0;
            Q0 = qSketchRegion(id + "F32", true);
            extrude(context, id + "F33", {"entities" : qUnion([Q0]), "endBound" : BoundingType.UP_TO_NEXT, "oppositeDirection" : true, "depth" : 25.4 * mm});
        }
        {
            var Q0;
            Q0=makeQuery(id+"F33.opExtrude","SWEPT_BODY",BODY,{"disambiguationData":[OSD([sQuery(id+"F32.wireOp",EDGE,"E136.bottom"),sQuery(id+"F32.wireOp",EDGE,"E136.top"),sQuery(id+"F32.wireOp",EDGE,"E136.left"),sQuery(id+"F32.wireOp",EDGE,"E136.right")])]});
            var Q1;
            Q1=makeQuery(id+"F13.opPattern","COPY",BODY,{"derivedFrom":makeQuery(id+"F12.opExtrude","SWEPT_BODY",BODY,{"disambiguationData":[OSD([sQuery(id+"F11.wireOp",EDGE,"E87.0"),sQuery(id+"F11.wireOp",EDGE,"E88.0"),sQuery(id+"F11.wireOp",EDGE,"E89"),sQuery(id+"F11.wireOp",EDGE,"E90"),sQuery(id+"F11.wireOp",EDGE,"E91"),sQuery(id+"F11.wireOp",EDGE,"E92")])]}),"instanceName":"1"});
            var Q2;
            Q2=makeQuery(id+"F30.opExtrude","SWEPT_BODY",BODY,{"disambiguationData":[OSD([sQuery(id+"F29.wireOp",EDGE,"E135.bottom"),sQuery(id+"F29.wireOp",EDGE,"E135.top"),sQuery(id+"F29.wireOp",EDGE,"E135.left"),sQuery(id+"F29.wireOp",EDGE,"E135.right")])]});
            booleanBodies(context, id + "F34", {"operationType" : BooleanOperationType.SUBTRACTION, "tools" : qUnion([Q0]), "targets" : qUnion([Q1, Q2]), "keepTools" : true});
        }
        {
            var Q0;
            Q0=qCreatedBy(id+"F2.planeOp",FACE);
            var sketch = newSketch(context, id + "F35", { "sketchPlane" : qUnion([Q0])});
            skLineSegment(sketch, "E137.0", {"start": v(15.88, 76.2) * mm, "end": v(390.53, 76.2) * mm});
            skLineSegment(sketch, "E137.1", {"start": v(390.53, 15.88) * mm, "end": v(15.88, 15.88) * mm});
            skLineSegment(sketch, "E137.2", {"start": v(15.88, 15.88) * mm, "end": v(15.88, 76.2) * mm});
            skLineSegment(sketch, "E137.3", {"start": v(390.53, 15.88) * mm, "end": v(390.53, 76.2) * mm});
            skPoint(sketch, "E138.orphan", {"position": v(15.88, 89.68) * mm});
            skPoint(sketch, "E139.orphan", {"position": v(15.88, 0) * mm});
            skPoint(sketch, "E140.orphan", {"position": v(390.53, 0) * mm});
            skPoint(sketch, "E141.orphan", {"position": v(390.53, 89.68) * mm});
            skSolve(sketch);
        }
        {
            var Q0;
            Q0 = qSketchRegion(id + "F35", true);
            extrude(context, id + "F36", {"entities" : qUnion([Q0]), "depth" : 9.52 * mm});
        }
        {
            var Q0;
            Q0=qCreatedBy(id+"F2.planeOp",FACE);
            cPlane(context, id + "F37", {"entities" : qUnion([Q0]), "cplaneType" : CPlaneType.OFFSET, "offset" : 177.8 * mm, "width" : 152.4 * mm, "height" : 152.4 * mm});
        }
        {
            var Q0;
            Q0=qCreatedBy(id+"F37.planeOp",FACE);
            var sketch = newSketch(context, id + "F38", { "sketchPlane" : qUnion([Q0])});
            skLineSegment(sketch, "E142.0.0", {"start": v(390.53, 76.2) * mm, "end": v(15.88, 76.2) * mm});
            skLineSegment(sketch, "E142.0.1", {"start": v(15.88, 76.2) * mm, "end": v(15.88, 15.88) * mm});
            skLineSegment(sketch, "E142.0.2", {"start": v(15.88, 15.88) * mm, "end": v(390.53, 15.88) * mm});
            skLineSegment(sketch, "E142.0.3", {"start": v(390.53, 15.88) * mm, "end": v(390.53, 76.2) * mm});
            skSolve(sketch);
        }
        {
            var Q0;
            Q0=makeQuery(id+"F38.imprint","IMPRINT",FACE,{"disambiguationData":[TD([[makeQuery(id+"F38.imprint","IMPRINT",EDGE,{"derivedFrom":sQuery(id+"F38.wireOp",EDGE,"E142.0.0")}),1.0]])]});
            extrude(context, id + "F39", {"entities" : qUnion([Q0]), "oppositeDirection" : true, "depth" : 15.88 * mm});
        }
        {
            var Q0;
            Q0=makeQuery(id+"F39.opExtrude","SWEPT_FACE",FACE,{"disambiguationData":[OSD([sQuery(id+"F38.wireOp",EDGE,"E142.0.3")])]});
            var sketch = newSketch(context, id + "F40", { "sketchPlane" : qUnion([Q0])});
            skLineSegment(sketch, "E143.bottom", {"start": v(-381, 76.2) * mm, "end": v(-203.2, 76.2) * mm});
            skLineSegment(sketch, "E143.top", {"start": v(-381, 15.88) * mm, "end": v(-203.2, 15.88) * mm});
            skLineSegment(sketch, "E143.left", {"start": v(-381, 76.2) * mm, "end": v(-381, 15.88) * mm});
            skLineSegment(sketch, "E143.right", {"start": v(-203.2, 76.2) * mm, "end": v(-203.2, 15.88) * mm});
            skSolve(sketch);
        }
        {
            var Q0;
            Q0 = qSketchRegion(id + "F40", true);
            extrude(context, id + "F41", {"entities" : qUnion([Q0]), "oppositeDirection" : true, "depth" : 9.52 * mm});
        }
        {
            var Q0;
            Q0=makeQuery(id+"F41.opExtrude","SWEPT_BODY",BODY,{"disambiguationData":[OSD([sQuery(id+"F40.wireOp",EDGE,"E143.bottom"),sQuery(id+"F40.wireOp",EDGE,"E143.top"),sQuery(id+"F40.wireOp",EDGE,"E143.left"),sQuery(id+"F40.wireOp",EDGE,"E143.right")])]});
            var Q1;
            Q1=qCreatedBy(id+"F10.planeOp",FACE);
            mirror(context, id + "F42", {"entities" : qUnion([Q0]), "mirrorPlane" : qUnion([Q1])});
        }
        {
            var Q0;
            Q0=makeQuery(id+"F39.opExtrude","SWEPT_FACE",FACE,{"disambiguationData":[OSD([sQuery(id+"F38.wireOp",EDGE,"E142.0.2")])]});
            var sketch = newSketch(context, id + "F43", { "sketchPlane" : qUnion([Q0])});
            skLineSegment(sketch, "E144.0", {"start": v(25.4, 365.13) * mm, "end": v(381, 365.13) * mm});
            skLineSegment(sketch, "E144.1", {"start": v(25.4, 365.13) * mm, "end": v(25.4, 212.73) * mm});
            skLineSegment(sketch, "E144.2", {"start": v(381, 212.73) * mm, "end": v(25.4, 212.73) * mm});
            skLineSegment(sketch, "E144.3", {"start": v(381, 365.13) * mm, "end": v(381, 212.73) * mm});
            skPoint(sketch, "E145.orphan", {"position": v(25.4, 381) * mm});
            skPoint(sketch, "E146.orphan", {"position": v(15.88, 365.13) * mm});
            skPoint(sketch, "E147.orphan", {"position": v(381, 381) * mm});
            skPoint(sketch, "E148.orphan", {"position": v(390.53, 365.13) * mm});
            skPoint(sketch, "E149.orphan", {"position": v(390.53, 212.73) * mm});
            skPoint(sketch, "E150.orphan", {"position": v(381, 203.2) * mm});
            skPoint(sketch, "E151.orphan", {"position": v(25.4, 203.2) * mm});
            skPoint(sketch, "E152.orphan", {"position": v(15.88, 212.73) * mm});
            skLineSegment(sketch, "E153.0", {"start": v(20.64, 369.89) * mm, "end": v(20.64, 207.96) * mm});
            skLineSegment(sketch, "E153.1", {"start": v(20.64, 369.89) * mm, "end": v(385.76, 369.89) * mm});
            skLineSegment(sketch, "E153.2", {"start": v(385.76, 369.89) * mm, "end": v(385.76, 207.96) * mm});
            skLineSegment(sketch, "E153.3", {"start": v(385.76, 207.96) * mm, "end": v(20.64, 207.96) * mm});
            skSolve(sketch);
        }
        {
            var Q0;
            Q0 = qSketchRegion(id + "F43", true);
            var Q1;
            Q1=makeQuery(id+"F43.imprint","IMPRINT",FACE,{"disambiguationData":[TD([[makeQuery(id+"F43.imprint","IMPRINT",EDGE,{"derivedFrom":sQuery(id+"F43.wireOp",EDGE,"E144.0")}),-1.0]])]});
            extrude(context, id + "F44", {"entities" : qUnion([Q0, Q1]), "oppositeDirection" : true, "depth" : 6.35 * mm});
        }
        {
            var Q0;
            Q0 = qSketchRegion(id + "F43", true);
            extrude(context, id + "F45", {"entities" : qUnion([Q0]), "operationType" : NewBodyOperationType.REMOVE, "oppositeDirection" : true, "depth" : 3.17 * mm});
        }
        {
            var Q0;
            Q0=makeQuery(id+"F44.opExtrude","SWEPT_BODY",BODY,{"disambiguationData":[OSD([sQuery(id+"F43.wireOp",EDGE,"E153.0"),sQuery(id+"F43.wireOp",EDGE,"E153.1"),sQuery(id+"F43.wireOp",EDGE,"E153.2"),sQuery(id+"F43.wireOp",EDGE,"E153.3")])]});
            var Q1;
            Q1=makeQuery(id+"F42.opPattern","COPY",BODY,{"derivedFrom":makeQuery(id+"F41.opExtrude","SWEPT_BODY",BODY,{"disambiguationData":[OSD([sQuery(id+"F40.wireOp",EDGE,"E143.bottom"),sQuery(id+"F40.wireOp",EDGE,"E143.top"),sQuery(id+"F40.wireOp",EDGE,"E143.left"),sQuery(id+"F40.wireOp",EDGE,"E143.right")])]}),"instanceName":"1"});
            var Q2;
            Q2=makeQuery(id+"F41.opExtrude","SWEPT_BODY",BODY,{"disambiguationData":[OSD([sQuery(id+"F40.wireOp",EDGE,"E143.bottom"),sQuery(id+"F40.wireOp",EDGE,"E143.top"),sQuery(id+"F40.wireOp",EDGE,"E143.left"),sQuery(id+"F40.wireOp",EDGE,"E143.right")])]});
            var Q3;
            Q3=makeQuery(id+"F36.opExtrude","SWEPT_BODY",BODY,{"disambiguationData":[OSD([sQuery(id+"F35.wireOp",EDGE,"E137.0"),sQuery(id+"F35.wireOp",EDGE,"E137.1"),sQuery(id+"F35.wireOp",EDGE,"E137.2"),sQuery(id+"F35.wireOp",EDGE,"E137.3")])]});
            var Q4;
            Q4=makeQuery(id+"F39.opExtrude","SWEPT_BODY",BODY,{"disambiguationData":[OSD([sQuery(id+"F38.wireOp",EDGE,"E142.0.0"),sQuery(id+"F38.wireOp",EDGE,"E142.0.1"),sQuery(id+"F38.wireOp",EDGE,"E142.0.2"),sQuery(id+"F38.wireOp",EDGE,"E142.0.3")])]});
            booleanBodies(context, id + "F46", {"operationType" : BooleanOperationType.SUBTRACTION, "tools" : qUnion([Q0]), "targets" : qUnion([Q1, Q2, Q3, Q4]), "keepTools" : true});
        }
        {
            var Q0;
            Q0=makeQuery(id+"F41.opExtrude","SWEPT_BODY",BODY,{"disambiguationData":[OSD([sQuery(id+"F40.wireOp",EDGE,"E143.bottom"),sQuery(id+"F40.wireOp",EDGE,"E143.top"),sQuery(id+"F40.wireOp",EDGE,"E143.left"),sQuery(id+"F40.wireOp",EDGE,"E143.right")])]});
            var Q1;
            Q1=makeQuery(id+"F39.opExtrude","CAP_EDGE",EDGE,{"disambiguationData":[OSD([sQuery(id+"F38.wireOp",EDGE,"E142.0.0")])],"isStart":true});
            transform(context, id + "F47", {"entities" : qUnion([Q0]), "transformType" : TransformType.TRANSLATION_DISTANCE, "transformDirection" : qUnion([Q1]), "distance" : 152.4 * mm, "oppositeDirection" : true, "makeCopy" : true});
        }
        {
            var Q0;
            Q0=makeQuery(id+"F47.opPattern","COPY",FACE,{"derivedFrom":makeQuery(id+"F41.opExtrude","CAP_FACE",FACE,{"disambiguationData":[OSD([sQuery(id+"F40.wireOp",EDGE,"E143.bottom"),sQuery(id+"F40.wireOp",EDGE,"E143.top"),sQuery(id+"F40.wireOp",EDGE,"E143.left"),sQuery(id+"F40.wireOp",EDGE,"E143.right")])],"isStart":true}),"instanceName":"1"});
            var sketch = newSketch(context, id + "F48", { "sketchPlane" : qUnion([Q0])});
            skLineSegment(sketch, "E154", {"start": v(-292.1, 15.88) * mm, "end": v(-292.1, 76.2) * mm, "construction": true});
            skLineSegment(sketch, "E155", {"start": v(-381, 76.2) * mm, "end": v(-381, 69.85) * mm});
            skLineSegment(sketch, "E156", {"start": v(-381, 69.85) * mm, "end": v(-365.13, 65.9) * mm});
            skLineSegment(sketch, "E157", {"start": v(-365.13, 65.9) * mm, "end": v(-365.13, 76.2) * mm});
            skLineSegment(sketch, "E158", {"start": v(-365.13, 76.2) * mm, "end": v(-381, 76.2) * mm});
            skPoint(sketch, "E159.start.orphan", {"position": v(-381, 46.04) * mm});
            skLineSegment(sketch, "E160", {"start": v(-381, 46.04) * mm, "end": v(-292.1, 46.04) * mm, "construction": true});
            skLineSegment(sketch, "E161.MirrorCS", {"start": v(-365.13, 15.88) * mm, "end": v(-381, 15.88) * mm});
            skLineSegment(sketch, "E162.MirrorCS", {"start": v(-381, 15.88) * mm, "end": v(-381, 22.23) * mm});
            skLineSegment(sketch, "E163.MirrorCS", {"start": v(-381, 22.23) * mm, "end": v(-365.13, 26.18) * mm});
            skLineSegment(sketch, "E164.MirrorCS", {"start": v(-365.13, 26.18) * mm, "end": v(-365.13, 15.88) * mm});
            skLineSegment(sketch, "E165", {"start": v(-381, 57.15) * mm, "end": v(-365.13, 61.1) * mm});
            skLineSegment(sketch, "E166", {"start": v(-365.13, 61.1) * mm, "end": v(-365.13, 45.14) * mm});
            skLineSegment(sketch, "E167", {"start": v(-381, 57.15) * mm, "end": v(-381, 46.04) * mm});
            skLineSegment(sketch, "E168.MirrorCS", {"start": v(-381, 34.93) * mm, "end": v(-365.13, 30.97) * mm});
            skLineSegment(sketch, "E169.MirrorCS", {"start": v(-365.13, 30.97) * mm, "end": v(-365.13, 46.94) * mm});
            skLineSegment(sketch, "E170.MirrorCS", {"start": v(-381, 34.93) * mm, "end": v(-381, 46.04) * mm});
            skPoint(sketch, "E171.MirrorP", {"position": v(-203.2, 46.04) * mm});
            skLineSegment(sketch, "E172.MirrorCS", {"start": v(-203.2, 76.2) * mm, "end": v(-203.2, 69.85) * mm});
            skLineSegment(sketch, "E173.MirrorCS", {"start": v(-203.2, 57.15) * mm, "end": v(-203.2, 46.04) * mm});
            skLineSegment(sketch, "E174.MirrorCS", {"start": v(-203.2, 34.93) * mm, "end": v(-203.2, 46.04) * mm});
            skLineSegment(sketch, "E175.MirrorCS", {"start": v(-203.2, 15.88) * mm, "end": v(-203.2, 22.23) * mm});
            skLineSegment(sketch, "E176", {"start": v(-212.73, 76.2) * mm, "end": v(-203.2, 76.2) * mm});
            skLineSegment(sketch, "E177", {"start": v(-203.2, 69.85) * mm, "end": v(-212.73, 67.48) * mm});
            skLineSegment(sketch, "E178", {"start": v(-212.73, 67.48) * mm, "end": v(-212.73, 76.2) * mm});
            skLineSegment(sketch, "E179", {"start": v(-203.2, 57.15) * mm, "end": v(-212.73, 59.52) * mm});
            skLineSegment(sketch, "E180", {"start": v(-212.73, 59.52) * mm, "end": v(-212.73, 32.55) * mm});
            skLineSegment(sketch, "E181", {"start": v(-212.73, 32.55) * mm, "end": v(-203.2, 34.92) * mm});
            skLineSegment(sketch, "E182", {"start": v(-203.2, 22.23) * mm, "end": v(-212.73, 24.6) * mm});
            skLineSegment(sketch, "E183", {"start": v(-212.73, 24.6) * mm, "end": v(-212.73, 15.88) * mm});
            skLineSegment(sketch, "E184", {"start": v(-212.73, 15.88) * mm, "end": v(-203.2, 15.88) * mm});
            skSolve(sketch);
        }
        {
            var Q0;
            Q0 = qSketchRegion(id + "F48", true);
            extrude(context, id + "F49", {"entities" : qUnion([Q0]), "operationType" : NewBodyOperationType.REMOVE, "oppositeDirection" : true, "depth" : 9.52 * mm});
        }
        {
            var Q0;
            Q0=makeQuery(id+"F41.opExtrude","SWEPT_BODY",BODY,{"disambiguationData":[OSD([sQuery(id+"F40.wireOp",EDGE,"E143.bottom"),sQuery(id+"F40.wireOp",EDGE,"E143.top"),sQuery(id+"F40.wireOp",EDGE,"E143.left"),sQuery(id+"F40.wireOp",EDGE,"E143.right")])]});
            var Q1;
            Q1=makeQuery(id+"F42.opPattern","COPY",BODY,{"derivedFrom":makeQuery(id+"F41.opExtrude","SWEPT_BODY",BODY,{"disambiguationData":[OSD([sQuery(id+"F40.wireOp",EDGE,"E143.bottom"),sQuery(id+"F40.wireOp",EDGE,"E143.top"),sQuery(id+"F40.wireOp",EDGE,"E143.left"),sQuery(id+"F40.wireOp",EDGE,"E143.right")])]}),"instanceName":"1"});
            deleteBodies(context, id + "F50", {"entities" : qUnion([Q0, Q1])});
        }
        {
            var Q0;
            Q0=makeQuery(id+"F47.opPattern","COPY",BODY,{"derivedFrom":makeQuery(id+"F41.opExtrude","SWEPT_BODY",BODY,{"disambiguationData":[OSD([sQuery(id+"F40.wireOp",EDGE,"E143.bottom"),sQuery(id+"F40.wireOp",EDGE,"E143.top"),sQuery(id+"F40.wireOp",EDGE,"E143.left"),sQuery(id+"F40.wireOp",EDGE,"E143.right")])]}),"instanceName":"1"});
            var Q1;
            Q1=makeQuery(id+"F39.opExtrude","CAP_EDGE",EDGE,{"disambiguationData":[OSD([sQuery(id+"F38.wireOp",EDGE,"E142.0.0")])],"isStart":true});
            transform(context, id + "F51", {"entities" : qUnion([Q0]), "transformType" : TransformType.TRANSLATION_DISTANCE, "transformDirection" : qUnion([Q1]), "distance" : 152.4 * mm, "makeCopy" : false});
        }
        {
            var Q0;
            Q0=makeQuery(id+"F47.opPattern","COPY",BODY,{"derivedFrom":makeQuery(id+"F41.opExtrude","SWEPT_BODY",BODY,{"disambiguationData":[OSD([sQuery(id+"F40.wireOp",EDGE,"E143.bottom"),sQuery(id+"F40.wireOp",EDGE,"E143.top"),sQuery(id+"F40.wireOp",EDGE,"E143.left"),sQuery(id+"F40.wireOp",EDGE,"E143.right")])]}),"instanceName":"1"});
            var Q1;
            Q1=makeQuery(id+"F39.opExtrude","SWEPT_BODY",BODY,{"disambiguationData":[OSD([sQuery(id+"F38.wireOp",EDGE,"E142.0.0"),sQuery(id+"F38.wireOp",EDGE,"E142.0.1"),sQuery(id+"F38.wireOp",EDGE,"E142.0.2"),sQuery(id+"F38.wireOp",EDGE,"E142.0.3")])]});
            var Q2;
            Q2=makeQuery(id+"F36.opExtrude","SWEPT_BODY",BODY,{"disambiguationData":[OSD([sQuery(id+"F35.wireOp",EDGE,"E137.0"),sQuery(id+"F35.wireOp",EDGE,"E137.1"),sQuery(id+"F35.wireOp",EDGE,"E137.2"),sQuery(id+"F35.wireOp",EDGE,"E137.3")])]});
            booleanBodies(context, id + "F52", {"operationType" : BooleanOperationType.SUBTRACTION, "tools" : qUnion([Q0]), "targets" : qUnion([Q1, Q2]), "keepTools" : true});
        }
        {
            var Q0;
            Q0=makeQuery(id+"F47.opPattern","COPY",BODY,{"derivedFrom":makeQuery(id+"F41.opExtrude","SWEPT_BODY",BODY,{"disambiguationData":[OSD([sQuery(id+"F40.wireOp",EDGE,"E143.bottom"),sQuery(id+"F40.wireOp",EDGE,"E143.top"),sQuery(id+"F40.wireOp",EDGE,"E143.left"),sQuery(id+"F40.wireOp",EDGE,"E143.right")])]}),"instanceName":"1"});
            var Q1;
            Q1=qCreatedBy(id+"F10.planeOp",FACE);
            mirror(context, id + "F53", {"entities" : qUnion([Q0]), "mirrorPlane" : qUnion([Q1])});
        }
        {
            var Q0;
            Q0=makeQuery(id+"F53.opPattern","COPY",BODY,{"derivedFrom":makeQuery(id+"F47.opPattern","COPY",BODY,{"derivedFrom":makeQuery(id+"F41.opExtrude","SWEPT_BODY",BODY,{"disambiguationData":[OSD([sQuery(id+"F40.wireOp",EDGE,"E143.bottom"),sQuery(id+"F40.wireOp",EDGE,"E143.top"),sQuery(id+"F40.wireOp",EDGE,"E143.left"),sQuery(id+"F40.wireOp",EDGE,"E143.right")])]}),"instanceName":"1"}),"instanceName":"1"});
            var Q1;
            Q1=makeQuery(id+"F39.opExtrude","SWEPT_BODY",BODY,{"disambiguationData":[OSD([sQuery(id+"F38.wireOp",EDGE,"E142.0.0"),sQuery(id+"F38.wireOp",EDGE,"E142.0.1"),sQuery(id+"F38.wireOp",EDGE,"E142.0.2"),sQuery(id+"F38.wireOp",EDGE,"E142.0.3")])]});
            var Q2;
            Q2=makeQuery(id+"F36.opExtrude","SWEPT_BODY",BODY,{"disambiguationData":[OSD([sQuery(id+"F35.wireOp",EDGE,"E137.0"),sQuery(id+"F35.wireOp",EDGE,"E137.1"),sQuery(id+"F35.wireOp",EDGE,"E137.2"),sQuery(id+"F35.wireOp",EDGE,"E137.3")])]});
            booleanBodies(context, id + "F54", {"operationType" : BooleanOperationType.SUBTRACTION, "tools" : qUnion([Q0]), "targets" : qUnion([Q1, Q2]), "keepTools" : true});
        }
        {
            var Q0;
            Q0=makeQuery(id+"F44.opExtrude","SWEPT_BODY",BODY,{"disambiguationData":[OSD([sQuery(id+"F43.wireOp",EDGE,"E153.0"),sQuery(id+"F43.wireOp",EDGE,"E153.1"),sQuery(id+"F43.wireOp",EDGE,"E153.2"),sQuery(id+"F43.wireOp",EDGE,"E153.3")])]});
            var Q1;
            Q1=makeQuery(id+"F53.opPattern","COPY",BODY,{"derivedFrom":makeQuery(id+"F47.opPattern","COPY",BODY,{"derivedFrom":makeQuery(id+"F41.opExtrude","SWEPT_BODY",BODY,{"disambiguationData":[OSD([sQuery(id+"F40.wireOp",EDGE,"E143.bottom"),sQuery(id+"F40.wireOp",EDGE,"E143.top"),sQuery(id+"F40.wireOp",EDGE,"E143.left"),sQuery(id+"F40.wireOp",EDGE,"E143.right")])]}),"instanceName":"1"}),"instanceName":"1"});
            var Q2;
            Q2=makeQuery(id+"F47.opPattern","COPY",BODY,{"derivedFrom":makeQuery(id+"F41.opExtrude","SWEPT_BODY",BODY,{"disambiguationData":[OSD([sQuery(id+"F40.wireOp",EDGE,"E143.bottom"),sQuery(id+"F40.wireOp",EDGE,"E143.top"),sQuery(id+"F40.wireOp",EDGE,"E143.left"),sQuery(id+"F40.wireOp",EDGE,"E143.right")])]}),"instanceName":"1"});
            booleanBodies(context, id + "F55", {"operationType" : BooleanOperationType.SUBTRACTION, "tools" : qUnion([Q0]), "targets" : qUnion([Q1, Q2]), "keepTools" : true});
        }
    });
